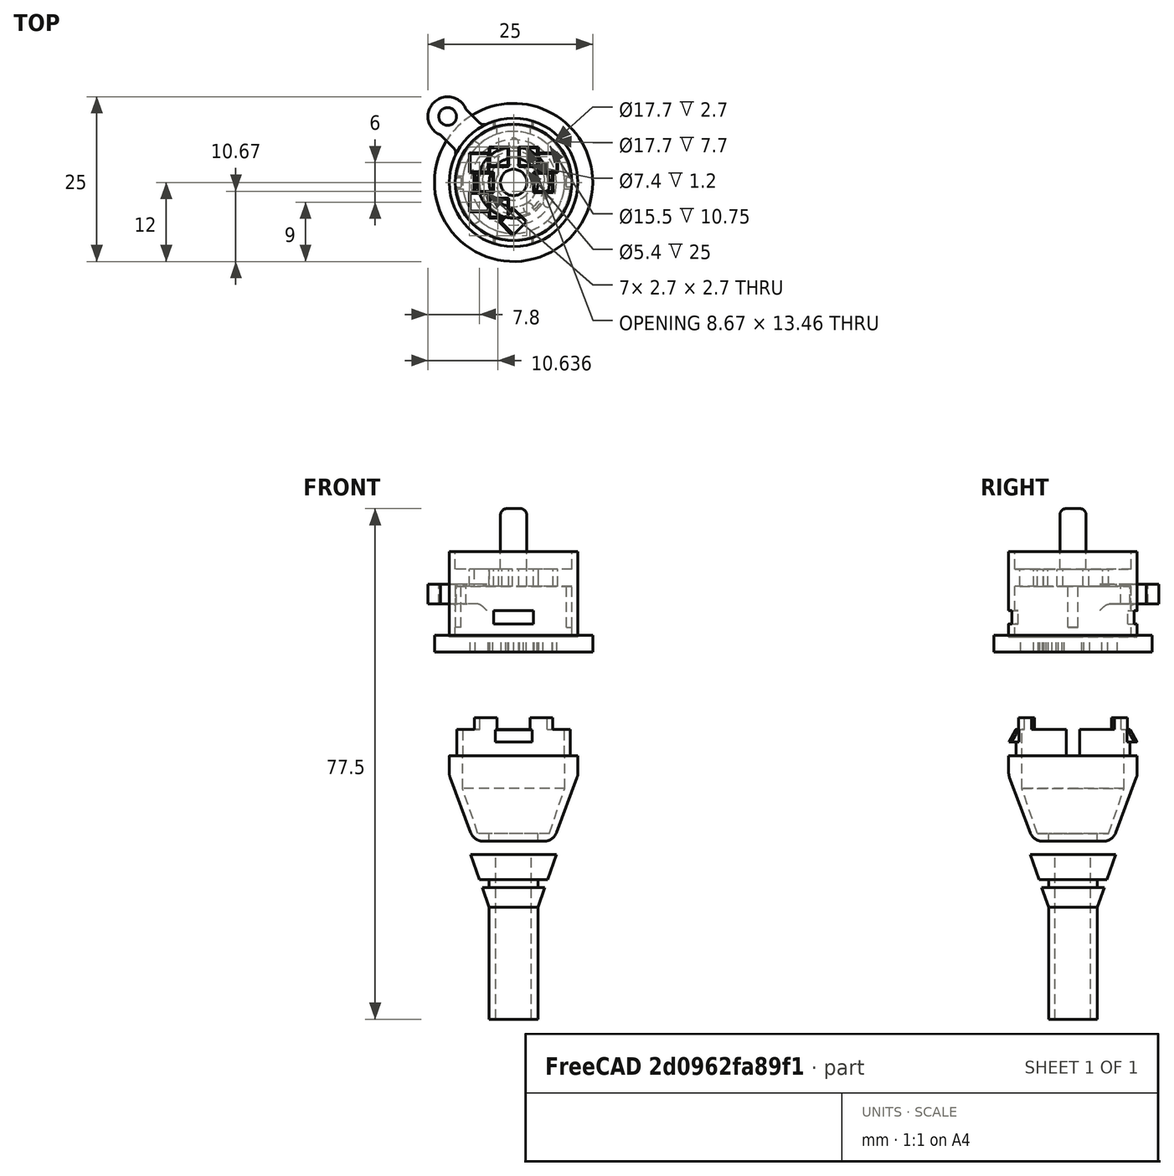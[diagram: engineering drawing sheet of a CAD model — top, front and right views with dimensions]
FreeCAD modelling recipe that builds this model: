
FCSTD DOCUMENT  (FreeCAD 0.18RUnknown)
Label: microphone-connector
License: All rights reserved
LicenseURL: http://en.wikipedia.org/wiki/All_rights_reserved
objects: Part::Box×28, Part::Cylinder×21, Part::Cut×13, Part::MultiFuse×13, Part::Cone×4, Mesh::Feature×4, Part::Fillet×3, Part::Compound×2, Part::FeaturePython×1, Part::MultiCommon×1, App::Part×1, App::VRMLObject×1
note: 86 computed .brp shape members not serialized (recipe doc carries the construction recipe); baked Part::Feature solids carry a one-line shape summary decoded from their .brp

FEATURE [Part::Cylinder] Cylinder001  label="Locator Pin"
  Angle = 360
  AttacherType = Attacher::AttachEngine3D
  Height = 10.5
  Placement = pos=(0,0,4) rot=(0,0,1;0rad)
  Radius = 2
FEATURE [Part::Box] Box  label="Cube"
  AttacherType = Attacher::AttachEngine3D
  Height = 3
  Length = 6
  Placement = pos=(-3.0052,6.89429,0) rot=(0,0,1;2.35619rad)
  Width = 5.5
FEATURE [Part::Cylinder] Cylinder022
  Angle = 360
  AttacherType = Attacher::AttachEngine3D
  Height = 15
  Placement = pos=(0,0,-6) rot=(0,0,1;0rad)
  Radius = 8.85
FEATURE [Part::Cylinder] Cylinder002  label="Attachement Point"
  Angle = 360
  AttacherType = Attacher::AttachEngine3D
  Height = 3
  Placement = pos=(-10.0024,10.0024,0) rot=(0,0,-1;1.5708rad)
  Radius = 3
FEATURE [Part::Cylinder] Cylinder019
  Angle = 360
  AttacherType = Attacher::AttachEngine3D
  Height = 5
  Placement = pos=(-10.0024,10.0024,0) rot=(0,0,-1;1.5708rad)
  Radius = 1.35
FEATURE [Part::Cylinder] Cylinder018  label="Negative"
  Angle = 360
  AttacherType = Attacher::AttachEngine3D
  Height = 13
  Placement = pos=(0,0,-5) rot=(0,0,1;0rad)
  Radius = 8.85
FEATURE [Part::Cylinder] Cylinder017  label="Positive"
  Angle = 360
  AttacherType = Attacher::AttachEngine3D
  Height = 13
  Placement = pos=(0,0,-5) rot=(0,0,1;0rad)
  Radius = 9.75
FEATURE [Part::Cut] Cut008  label="Outer Wall"
  Base = -> Cylinder017
  Tool = -> Cylinder018
FEATURE [Part::MultiFuse] Fusion008
  Shapes = -> [Box,Cylinder002,Cut008]
FEATURE [Part::Cut] Cut
  Base = -> Fusion008
  Tool = -> Cylinder019
FEATURE [Part::Cut] Cut009
  Base = -> Cut
  Tool = -> Cylinder022
FEATURE [Part::FeaturePython] Connect  # WARN: FeaturePython — macro-defined, semantics opaque (R4)
  Objects = -> [Cut009]
  Tolerance = 0
FEATURE [Part::Box] Box004  label="Cube004"
  AttacherType = Attacher::AttachEngine3D
  Height = 7.7
  Length = 1
  Placement = pos=(8,-0.75,-3.5) rot=(0,0,1;0rad)
  Width = 1.5
FEATURE [Part::Box] Box005  label="Cube005"
  AttacherType = Attacher::AttachEngine3D
  Height = 7.7
  Length = 1
  Placement = pos=(-8,0.75,-3.5) rot=(0,0,1;3.14159rad)
  Width = 1.5
FEATURE [Part::Fillet] Fillet
  Base = -> Cylinder001
  Edges = 1 edges r=1: [Edge1]
FEATURE [Part::Box] Box006  label="Cube006"
  AttacherType = Attacher::AttachEngine3D
  Height = 2
  Length = 6
  Placement = pos=(-3,-10,-3) rot=(0,0,1;0rad)
  Width = 20
FEATURE [Part::Box] Box007  label="Cube007"
  AttacherType = Attacher::AttachEngine3D
  Height = 1.8
  Length = 5.6
  Placement = pos=(-2.8,-10,-7.9) rot=(0,0,1;0rad)
  Width = 20
FEATURE [Part::Cone] Cone002
  Angle = 360
  AttacherType = Attacher::AttachEngine3D
  Height = 2
  Placement = pos=(0,0,-8) rot=(0,0,1;0rad)
  Radius1 = 9.75
  Radius2 = 8.65
FEATURE [Part::MultiCommon] Common
  Shapes = -> [Cone002,Box007]
FEATURE [Part::Cylinder] Cylinder035  label="Cylinder033"
  Angle = 360
  AttacherType = Attacher::AttachEngine3D
  Height = 11
  Placement = pos=(0,0,-9) rot=(0,0,1;0rad)
  Radius = 7.3
FEATURE [Part::Cut] Cut013002  label="Clips"
  Base = -> Common
  Placement = pos=(0,0,5) rot=(0,0,1;0rad)
  Tool = -> Cylinder035
FEATURE [Part::Cylinder] Cylinder
  Angle = 360
  AttacherType = Attacher::AttachEngine3D
  Height = 5.75
  Placement = pos=(0,0,-5) rot=(0,0,1;0rad)
  Radius = 8.65
FEATURE [Part::Cylinder] Cylinder036  label="Cylinder034"
  Angle = 360
  AttacherType = Attacher::AttachEngine3D
  Height = 11
  Placement = pos=(0,0,-10) rot=(0,0,1;0rad)
  Radius = 7.75
FEATURE [Part::Cylinder] Cylinder037  label="Cylinder035"
  Angle = 360
  AttacherType = Attacher::AttachEngine3D
  Height = 3
  Placement = pos=(0,0,-8) rot=(0,0,1;0rad)
  Radius = 9.75
FEATURE [Part::Cone] Cone
  Angle = 360
  AttacherType = Attacher::AttachEngine3D
  Height = 10
  Placement = pos=(0,0,-18) rot=(0,0,1;0rad)
  Radius1 = 6
  Radius2 = 9.75
FEATURE [Part::Cone] Cone003
  Angle = 360
  AttacherType = Attacher::AttachEngine3D
  Height = 8
  Placement = pos=(0,0,-18) rot=(0,0,1;0rad)
  Radius1 = 5
  Radius2 = 7.75
FEATURE [Part::MultiFuse] Fusion014  label="Upper Exterior"
  Shapes = -> [Cone,Cut013002,Cylinder037,Cylinder]
FEATURE [Part::MultiFuse] Fusion015
  Shapes = -> [Cone003,Cylinder036]
FEATURE [Part::Cut] Cut013003  label="Body"
  Base = -> Fusion014
  Tool = -> Fusion015
FEATURE [Part::Cylinder] Cylinder038  label="Cylinder036"
  Angle = 360
  AttacherType = Attacher::AttachEngine3D
  Height = 1.2
  Placement = pos=(0,0,-18) rot=(0,0,1;0rad)
  Radius = 6
FEATURE [Part::Cylinder] Cylinder039  label="Cylinder037"
  Angle = 360
  AttacherType = Attacher::AttachEngine3D
  Height = 1.2
  Placement = pos=(0,0,-18) rot=(0,0,1;0rad)
  Radius = 3.7
FEATURE [Part::Cut] Cut013004  label="Top"
  Base = -> Cylinder038
  Tool = -> Cylinder039
FEATURE [Part::Cylinder] Cylinder040  label="Cylinder038"
  Angle = 360
  AttacherType = Attacher::AttachEngine3D
  Height = 1.2
  Placement = pos=(0,0,-18) rot=(0,0,1;0rad)
  Radius = 3.7
FEATURE [Part::Cylinder] Cylinder041  label="Cylinder039"
  Angle = 360
  AttacherType = Attacher::AttachEngine3D
  Height = 1.2
  Placement = pos=(0,0,-18) rot=(0,0,1;0rad)
  Radius = 6
FEATURE [Part::Cut] Cut013005
  Base = -> Cylinder041
  Tool = -> Cylinder040
FEATURE [Part::Cylinder] Cylinder042  label="Cylinder040"
  Angle = 360
  AttacherType = Attacher::AttachEngine3D
  Height = 25
  Placement = pos=(0,0,-38) rot=(0,0,1;0rad)
  Radius = 3.7
FEATURE [Part::Cone] Cone004
  Angle = 360
  AttacherType = Attacher::AttachEngine3D
  Height = 8
  Placement = pos=(0,0,-21) rot=(0,0,1;0rad)
  Radius1 = 3.7
  Radius2 = 6.5
FEATURE [Part::Cut] Cut013006
  Base = -> Cone004
  Tool = -> Cut013005
FEATURE [Part::MultiFuse] Fusion017
  Shapes = -> [Cut013006,Cylinder042]
FEATURE [Part::Cylinder] Cylinder043  label="Cylinder041"
  Angle = 360
  AttacherType = Attacher::AttachEngine3D
  Height = 25
  Placement = pos=(0,0,-38) rot=(0,0,1;0rad)
  Radius = 2.7
FEATURE [Part::Cut] Cut013007  label="Connector Boot"
  Base = -> Fusion017
  Placement = pos=(0,0,-15) rot=(0,0,1;0rad)
  Tool = -> Cylinder043
FEATURE [Part::Box] Box008  label="Cube008"
  AttacherType = Attacher::AttachEngine3D
  Height = 6
  Length = 20
  Placement = pos=(-10,-1,-5) rot=(0,0,1;0rad)
  Width = 2
FEATURE [Part::Cylinder] Cylinder044  label="Cylinder042"
  Angle = 360
  AttacherType = Attacher::AttachEngine3D
  Height = 2.6
  Placement = pos=(0,0,2.7) rot=(0,0,1;0rad)
  Radius = 9
FEATURE [Part::Box] Box009  label="Cube009"
  AttacherType = Attacher::AttachEngine3D
  Height = 2.8
  Length = 3
  Placement = pos=(-0.15,-8.06,2.6) rot=(0,0,1;0.785398rad)
  Width = 3
FEATURE [Part::Box] Box010  label="Cube010"
  AttacherType = Attacher::AttachEngine3D
  Height = 2.8
  Length = 3
  Placement = pos=(-3.75,-5.4,2.6) rot=(0,0,1;0rad)
  Width = 3
FEATURE [Part::Box] Box011  label="Cube011"
  AttacherType = Attacher::AttachEngine3D
  Height = 2.8
  Length = 3
  Placement = pos=(-6.7,-4.5,2.6) rot=(0,0,1;0rad)
  Width = 3
FEATURE [Part::Box] Box012  label="Cube012"
  AttacherType = Attacher::AttachEngine3D
  Height = 2.8
  Length = 3
  Placement = pos=(-6,-1.55,2.6) rot=(0,0,1;0rad)
  Width = 3.1
FEATURE [Part::Box] Box013  label="Cube013"
  AttacherType = Attacher::AttachEngine3D
  Height = 2.8
  Length = 3
  Placement = pos=(-6.7,1.5,2.6) rot=(0,0,1;0rad)
  Width = 3
FEATURE [Part::Box] Box014  label="Cube014"
  AttacherType = Attacher::AttachEngine3D
  Height = 2.8
  Length = 3
  Placement = pos=(0.75,2.4,2.6) rot=(0,0,1;0rad)
  Width = 3
FEATURE [Part::Box] Box015  label="Cube015"
  AttacherType = Attacher::AttachEngine3D
  Height = 2.8
  Length = 3
  Placement = pos=(3.7,1.5,2.6) rot=(0,0,1;0rad)
  Width = 3
FEATURE [Part::Box] Box016  label="Cube016"
  AttacherType = Attacher::AttachEngine3D
  Height = 2.8
  Length = 3
  Placement = pos=(3,-1.55,2.6) rot=(0,0,1;0rad)
  Width = 3.1
FEATURE [Part::Box] Box017  label="Cube017"
  AttacherType = Attacher::AttachEngine3D
  Height = 2.8
  Length = 3
  Placement = pos=(-3.75,2.4,2.6) rot=(0,0,1;0rad)
  Width = 3
FEATURE [Part::Box] Box018  label="Cube018"
  AttacherType = Attacher::AttachEngine3D
  Height = 2.8
  Length = 2.7
  Placement = pos=(-3.6,2.55,2.6) rot=(0,0,1;0rad)
  Width = 2.7
FEATURE [Part::Cylinder] Cylinder048  label="Cylinder046"
  Angle = 360
  AttacherType = Attacher::AttachEngine3D
  Height = 2.6
  Placement = pos=(0,0,2.7) rot=(0,0,1;0rad)
  Radius = 12
FEATURE [Part::Box] Box019  label="Cube019"
  AttacherType = Attacher::AttachEngine3D
  Height = 2.8
  Length = 2.7
  Placement = pos=(0,-7.91,2.6) rot=(0,0,1;0.785398rad)
  Width = 2.7
FEATURE [Part::Box] Box020  label="Cube020"
  AttacherType = Attacher::AttachEngine3D
  Height = 2.8
  Length = 2.7
  Placement = pos=(-3.6,-5.25,2.6) rot=(0,0,1;0rad)
  Width = 2.7
FEATURE [Part::Box] Box021  label="Cube021"
  AttacherType = Attacher::AttachEngine3D
  Height = 2.8
  Length = 2.7
  Placement = pos=(-6.55,-4.35,2.6) rot=(0,0,1;0rad)
  Width = 2.7
FEATURE [Part::Box] Box022  label="Cube022"
  AttacherType = Attacher::AttachEngine3D
  Height = 2.8
  Length = 2.7
  Placement = pos=(-5.85,-1.35,2.6) rot=(0,0,1;0rad)
  Width = 2.7
FEATURE [Part::Box] Box023  label="Cube023"
  AttacherType = Attacher::AttachEngine3D
  Height = 2.8
  Length = 2.7
  Placement = pos=(-6.55,1.65,2.6) rot=(0,0,1;0rad)
  Width = 2.7
FEATURE [Part::Box] Box024  label="Cube024"
  AttacherType = Attacher::AttachEngine3D
  Height = 2.8
  Length = 2.7
  Placement = pos=(0.9,2.55,2.6) rot=(0,0,1;0rad)
  Width = 2.7
FEATURE [Part::Box] Box025  label="Cube025"
  AttacherType = Attacher::AttachEngine3D
  Height = 2.8
  Length = 2.7
  Placement = pos=(3.85,1.65,2.6) rot=(0,0,1;0rad)
  Width = 2.7
FEATURE [Part::Box] Box026  label="Cube026"
  AttacherType = Attacher::AttachEngine3D
  Height = 2.8
  Length = 2.7
  Placement = pos=(3.15,-1.35,2.6) rot=(0,0,1;0rad)
  Width = 2.7
FEATURE [Part::MultiFuse] Fusion019
  Shapes = -> [Box020,Box019]
FEATURE [Part::Cylinder] Cylinder049  label="Cylinder050"
  Angle = 360
  AttacherType = Attacher::AttachEngine3D
  Height = 10
  Placement = pos=(5.2,-3,0) rot=(0,0,1;0rad)
  Radius = 0.75
FEATURE [Part::Cylinder] Cylinder050  label="Cylinder051"
  Angle = 360
  AttacherType = Attacher::AttachEngine3D
  Height = 10
  Placement = pos=(0,6,0) rot=(0,0,1;0rad)
  Radius = 0.75
FEATURE [Part::Cylinder] Cylinder051  label="Cylinder048"
  Angle = 360
  AttacherType = Attacher::AttachEngine3D
  Height = 10
  Placement = pos=(2.25,-3.9,0) rot=(0,0,1;0rad)
  Radius = 0.75
FEATURE [Part::Compound] Compound001
  Links = -> [Cylinder049,Box018,Box021,Box022,Box023,Box024,Box025,Box026,Fusion019,Cylinder050,Cylinder051]
FEATURE [Part::Cut] Cut013010  label="PCB Solder Jig"
  Base = -> Cylinder048
  Tool = -> Compound001
FEATURE [App::Part] Part  label="PCB Layout Jig"
  Group = -> [Box025,Box018,Box022,Box021,Cylinder049,Box019,Compound001,Cylinder048,Box023,Fusion019,Cylinder050,Box024,Cylinder051,Box026,Box020,Cut013010]
  Origin = -> Origin018
  Placement = pos=(0,0,30) rot=(0,0,1;0rad)
FEATURE [Part::Box] Box027  label="Cube027"
  AttacherType = Attacher::AttachEngine3D
  Height = 2
  Length = 20
  Placement = pos=(2.5,-10,-1) rot=(0,0,1;1.5708rad)
  Width = 5
FEATURE [Part::Box] Box028  label="Cube028"
  AttacherType = Attacher::AttachEngine3D
  Height = 2
  Length = 20
  Placement = pos=(9.91025,-2.83494,-1) rot=(0,0,1;2.61799rad)
  Width = 5
FEATURE [Part::Box] Box029  label="Cube029"
  AttacherType = Attacher::AttachEngine3D
  Height = 2
  Length = 20
  Placement = pos=(-7.41025,-7.16506,-1) rot=(0,0,1;0.523599rad)
  Width = 5
FEATURE [Part::Box] Box030  label="Cube030"
  AttacherType = Attacher::AttachEngine3D
  Height = 2
  Length = 20
  Placement = pos=(10,2.5,-1) rot=(0,0,1;3.14159rad)
  Width = 5
FEATURE [Part::MultiFuse] Fusion021
  Shapes = -> [Cut013003,Cut013004]
FEATURE [Part::Fillet] Fillet002
  Base = -> Fusion021
  Edges = 2 edges r=2: [Edge1,Edge3]
FEATURE [Part::MultiFuse] Fusion022
  Shapes = -> [Box008,Box029,Box027,Box028,Box030]
FEATURE [Part::Cut] Cut013011  label="Connector Body"
  Base = -> Fillet002
  Placement = pos=(0,0,-8) rot=(0,0,1;0rad)
  Tool = -> Fusion022
FEATURE [Part::MultiFuse] Fusion  label="PCB Locator"
  Shapes = -> [Box004,Box005]
FEATURE [Part::MultiFuse] Fusion024
  Shapes = -> [Fusion,Connect]
FEATURE [Part::Cut] Cut013012
  Base = -> Fusion024
  Tool = -> Box006
FEATURE [Part::Fillet] Fillet003
  Base = -> Cut013012
  Edges = 3 edges r=1: [Edge62,Edge63,Edge64]
FEATURE [Mesh::Feature] Mesh  label="Connector Boot (Meshed)"
FEATURE [Mesh::Feature] Mesh003  label="PCB Solder Jig (Meshed)"
FEATURE [Mesh::Feature] Mesh005  label="Connector Body (Meshed)"
FEATURE [Part::MultiFuse] Fusion026
  Shapes = -> [Box017,Box013,Box012,Box011,Box010,Box009]
FEATURE [Part::MultiFuse] Fusion027
  Shapes = -> [Box014,Box015,Box016]
FEATURE [Part::Compound] Compound
  Links = -> [Fusion026,Fusion027]
FEATURE [Part::Cut] Cut013013
  Base = -> Cylinder044
  Tool = -> Compound
FEATURE [Part::MultiFuse] Fusion023
  Shapes = -> [Fillet,Cut013013]
FEATURE [Part::MultiFuse] Fusion025  label="Connector Base"
  Placement = pos=(0,0,10) rot=(0,0,1;0rad)
  Shapes = -> [Fusion023,Fillet003]
FEATURE [Mesh::Feature] Mesh006  label="Connector Base (Meshed)"
FEATURE [App::VRMLObject] TK_X90_Programming  label="TK-X90-Programming"
  Placement = pos=(-150,-100,1.22e-14) rot=(1,0,0;3.14159rad)
  Resources = TK_X90_Programming/shapes3D/mill-max-310-13-101-41-001000.wrl | TK_X90_Programming/shapes3D/SOT-23.wrl | TK_X90_Programming/shapes3D/R_0603_1608Metric.wrl
